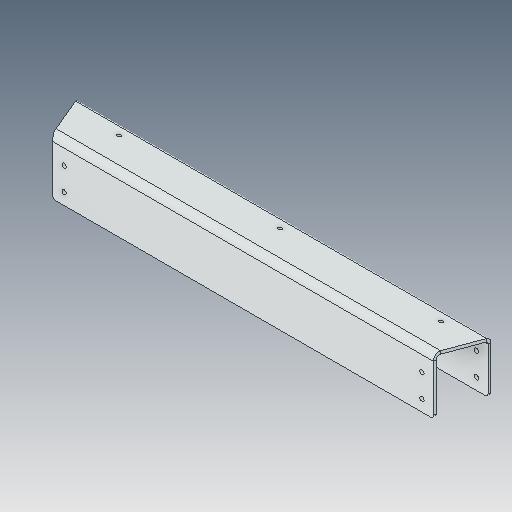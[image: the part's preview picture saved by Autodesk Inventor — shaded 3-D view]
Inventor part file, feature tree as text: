
AUTODESK INVENTOR PART (.ipt)
format: ipt  version: 2023.5 (Build 275446000, 446)  size: 143,872 bytes
history: native  units: in
note: dims shown in document units (in); Inventor stores cm internally (conversion verified against a paired STEP export)
features: fillet x1
ambient origin geometry x8: Origin, YZ Plane, XZ Plane, XY Plane, X Axis, Y Axis, Z Axis, Center Point
bodies: Solid1 (feature_tree)
feature tree (1):
  fillet  "Fillet1"  [1 undecoded]
note: 1 required parameter value undecoded (feature->parameter linkage not recoverable at this tier; creation-order binding heuristic only, values carry confidence <= 0.55)
